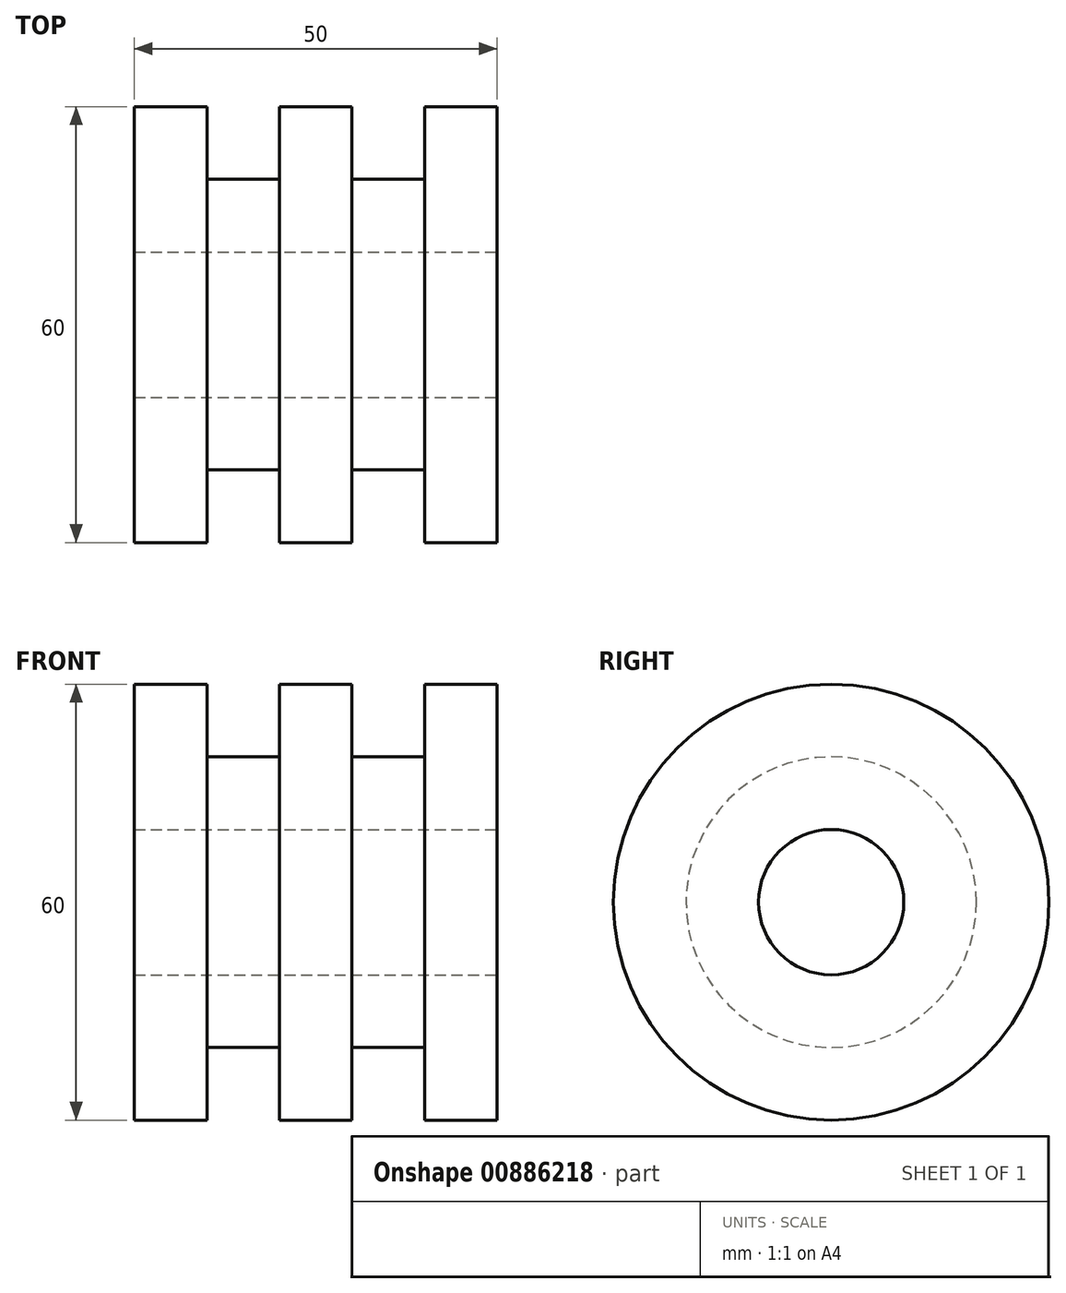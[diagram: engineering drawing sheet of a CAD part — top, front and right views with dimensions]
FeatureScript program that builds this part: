
annotation { "Feature Type Name" : "Feature", "Feature Type Description" : "" }
export const myFeature = defineFeature(function(context is Context, id is Id, definition is map)
    precondition{}
    {
        {
            var Q0;
            Q0=qCreatedBy(makeId("Top.planeOp"),FACE);
            var sketch = newSketch(context, id + "F0", { "sketchPlane" : qUnion([Q0])});
            skLineSegment(sketch, "E0.bottom", {"start": v(25, -15) * mm, "end": v(15, -15) * mm});
            skLineSegment(sketch, "E0.top", {"start": v(25, 15) * mm, "end": v(-25, 15) * mm});
            skLineSegment(sketch, "E0.left", {"start": v(25, -15) * mm, "end": v(25, 15) * mm});
            skLineSegment(sketch, "E0.right", {"start": v(-25, -15) * mm, "end": v(-25, 15) * mm});
            skPoint(sketch, "E0.middle", {"position": v(0, 0) * mm});
            skLineSegment(sketch, "E1", {"start": v(15, -15) * mm, "end": v(15, -5) * mm});
            skLineSegment(sketch, "E2", {"start": v(15, -5) * mm, "end": v(5, -5) * mm});
            skLineSegment(sketch, "E3", {"start": v(5, -5) * mm, "end": v(5, -15) * mm});
            skLineSegment(sketch, "E4", {"start": v(-25, -15) * mm, "end": v(-15, -15) * mm});
            skLineSegment(sketch, "E5", {"start": v(-15, -15) * mm, "end": v(-15, -5) * mm});
            skLineSegment(sketch, "E6", {"start": v(-15, -5) * mm, "end": v(-5, -5) * mm});
            skLineSegment(sketch, "E7", {"start": v(-5, -5) * mm, "end": v(-5, -15) * mm});
            skLineSegment(sketch, "E8.trimOffspring", {"start": v(5, -15) * mm, "end": v(-5, -15) * mm});
            skSolve(sketch);
        }
        {
            var Q0;
            Q0=makeQuery(id+"F0.imprint","IMPRINT",FACE,{"disambiguationData":[TD([[makeQuery(id+"F0.imprint","IMPRINT",EDGE,{"derivedFrom":sQuery(id+"F0.wireOp",EDGE,"E0.bottom")}),-1.0]])]});
            var Q1;
            Q1=sQuery(id+"F0.wireOp",EDGE,"E0.top");
            revolve(context, id + "F1", {"surfaceOperationType" : NewSurfaceOperationType.NEW, "entities" : qUnion([Q0]), "axis" : qUnion([Q1]), "revolveType" : RevolveType.FULL});
        }
        {
            var Q0;
            Q0=makeQuery(id+"F1.opRevolve","SWEPT_FACE",FACE,{"disambiguationData":[OSD([sQuery(id+"F0.wireOp",EDGE,"E0.left")])]});
            var sketch = newSketch(context, id + "F2", { "sketchPlane" : qUnion([Q0])});
            skCircle(sketch, "E9", {"center": v(15, 0) * mm, "radius": 10 * mm});
            skSolve(sketch);
        }
        {
            var Q0;
            Q0 = qSketchRegion(id + "F2", true);
            extrude(context, id + "F3", {"entities" : qUnion([Q0]), "operationType" : NewBodyOperationType.REMOVE, "oppositeDirection" : true, "depth" : 50 * mm, "offsetDistance" : 25 * mm});
        }
    });
